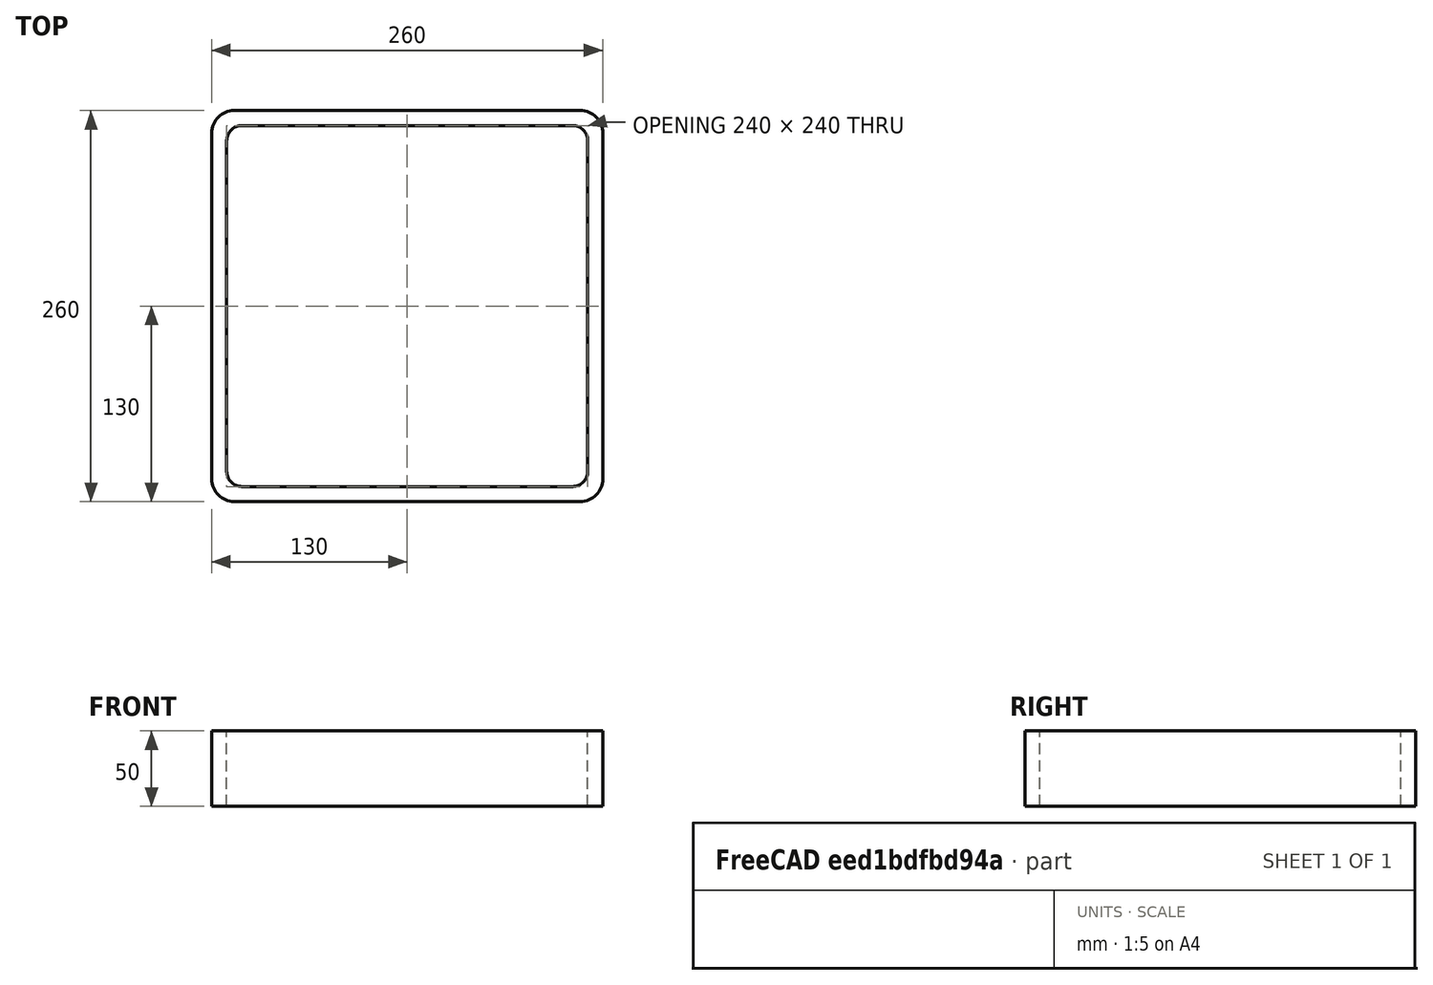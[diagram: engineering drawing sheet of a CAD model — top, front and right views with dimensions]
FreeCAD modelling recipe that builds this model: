
FCSTD DOCUMENT  (FreeCAD 0.15R4671 (Git))
Label: Square hollow section 260x260x10 EN10219 S235JRH
License: All rights reserved
LicenseURL: http://en.wikipedia.org/wiki/All_rights_reserved
objects: Sketcher::SketchObject×1, Part::Extrusion×1
note: 2 computed .brp shape members not serialized (recipe doc carries the construction recipe); baked Part::Feature solids carry a one-line shape summary decoded from their .brp

FEATURE [Sketcher::SketchObject] Sketch
  sketch-geometry (16):
    g0: LineSegment StartX=-110 StartY=120 StartZ=0 EndX=110 EndY=120 EndZ=0
    g1: LineSegment StartX=120 StartY=110 StartZ=0 EndX=120 EndY=-110 EndZ=0
    g2: LineSegment StartX=110 StartY=-120 StartZ=0 EndX=-110 EndY=-120 EndZ=0
    g3: LineSegment StartX=-120 StartY=-110 StartZ=0 EndX=-120 EndY=110 EndZ=0
    g4: LineSegment StartX=-115 StartY=130 StartZ=0 EndX=115 EndY=130 EndZ=0
    g5: LineSegment StartX=130 StartY=115 StartZ=0 EndX=130 EndY=-115 EndZ=0
    g6: LineSegment StartX=115 StartY=-130 StartZ=0 EndX=-115 EndY=-130 EndZ=0
    g7: LineSegment StartX=-130 StartY=-115 StartZ=0 EndX=-130 EndY=115 EndZ=0
    g8: ArcOfCircle CenterX=-110 CenterY=110 CenterZ=0 NormalX=0 NormalY=0 NormalZ=1 Radius=10 StartAngle=1.5708 EndAngle=3.14159
    g9: ArcOfCircle CenterX=110 CenterY=110 CenterZ=0 NormalX=0 NormalY=0 NormalZ=1 Radius=10 StartAngle=0 EndAngle=1.5708
    g10: ArcOfCircle CenterX=110 CenterY=-110 CenterZ=0 NormalX=0 NormalY=0 NormalZ=1 Radius=10 StartAngle=4.71239 EndAngle=6.28319
    g11: ArcOfCircle CenterX=-110 CenterY=-110 CenterZ=0 NormalX=0 NormalY=0 NormalZ=1 Radius=10 StartAngle=3.14159 EndAngle=4.71239
    g12: ArcOfCircle CenterX=115 CenterY=115 CenterZ=0 NormalX=0 NormalY=0 NormalZ=1 Radius=15 StartAngle=0 EndAngle=1.5708
    g13: ArcOfCircle CenterX=115 CenterY=-115 CenterZ=0 NormalX=0 NormalY=0 NormalZ=1 Radius=15 StartAngle=4.71239 EndAngle=6.28319
    g14: ArcOfCircle CenterX=-115 CenterY=-115 CenterZ=0 NormalX=0 NormalY=0 NormalZ=1 Radius=15 StartAngle=3.14159 EndAngle=4.71239
    g15: ArcOfCircle CenterX=-115 CenterY=115 CenterZ=0 NormalX=0 NormalY=0 NormalZ=1 Radius=15 StartAngle=1.5708 EndAngle=3.14159
  constraints (36):
    c: Horizontal(g2)
    c: Vertical(g3)
    c: Horizontal(g6)
    c: Vertical(g7)
    c: Tangent(g3,g8) = 1.5708
    c: Tangent(g0,g8) = 1.5708
    c: Tangent(g0,g9) = 1.5708
    c: Tangent(g1,g9) = 1.5708
    c: Tangent(g1,g10) = 1.5708
    c: Tangent(g2,g10) = 1.5708
    c: Tangent(g2,g11) = 1.5708
    c: Tangent(g3,g11) = 1.5708
    c: Tangent(g4,g12) = 1.5708
    c: Tangent(g5,g12) = 1.5708
    c: Tangent(g5,g13) = 1.5708
    c: Tangent(g6,g13) = 1.5708
    c: Tangent(g6,g14) = 1.5708
    c: Tangent(g7,g14) = 1.5708
    c: Tangent(g7,g15) = 1.5708
    c: Tangent(g4,g15) = 1.5708
    c: Equal(g9,g8)
    c: Equal(g9,g11)
    c: Equal(g9,g10)
    c: Equal(g12,g15)
    c: Equal(g12,g14)
    c: Equal(g12,g13)
    c: Symmetric(g4,g6,g-1)
    c: Symmetric(g7,g5,g-2)
    c: DistanceY(g4,g6) = -260
    c: DistanceX(g7,g5) = 260
    c: Symmetric(g3,g1,g-2)
    c: Symmetric(g0,g2,g-1)
    c: DistanceY(g0,g4) = 10
    c: DistanceX(g5,g1) = -10
    c: Radius(g9) = 10
    c: Radius(g12) = 15
FEATURE [Part::Extrusion] Extrude  label="Square hollow section 260x260x10 EN10219 S235JRH"
  Base = -> Sketch
  Dir = (0,0,50)
  Solid = true
